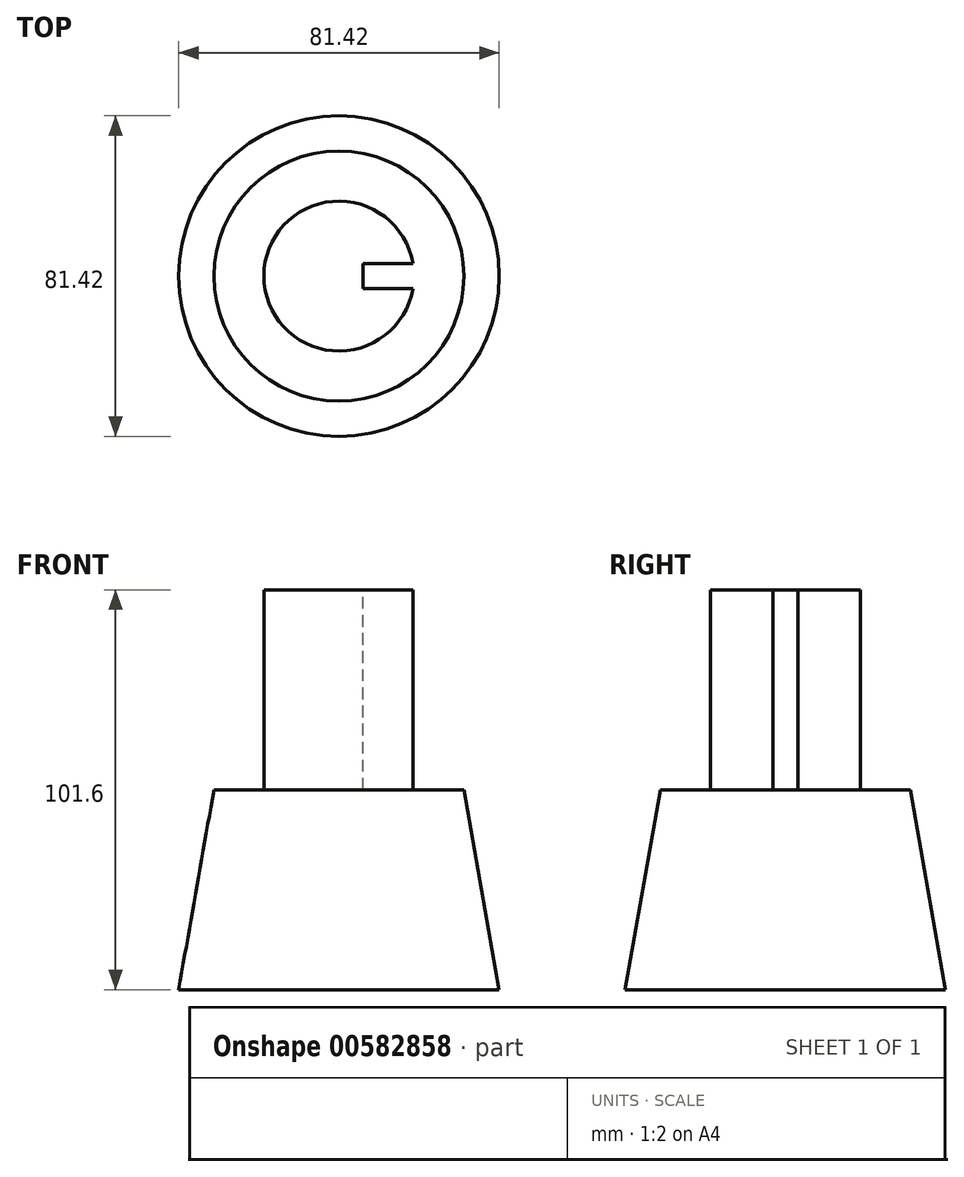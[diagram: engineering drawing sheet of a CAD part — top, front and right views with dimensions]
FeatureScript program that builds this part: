
annotation { "Feature Type Name" : "Feature", "Feature Type Description" : "" }
export const myFeature = defineFeature(function(context is Context, id is Id, definition is map)
    precondition{}
    {
        {
            var Q0;
            Q0=qCreatedBy(makeId("Front.planeOp"),FACE);
            var sketch = newSketch(context, id + "F0", { "sketchPlane" : qUnion([Q0])});
            skLineSegment(sketch, "E0", {"start": v(0, 76.2) * mm, "end": v(0, -76.2) * mm, "construction": true});
            skLineSegment(sketch, "E1", {"start": v(0, -76.2) * mm, "end": v(-25.4, -76.2) * mm});
            skLineSegment(sketch, "E2", {"start": v(-25.4, -76.2) * mm, "end": v(-25.4, 0) * mm});
            skLineSegment(sketch, "E3", {"start": v(-25.4, 0) * mm, "end": v(-22.23, 6.8) * mm});
            skLineSegment(sketch, "E4", {"start": v(-22.23, 6.8) * mm, "end": v(-22.23, 19.5) * mm});
            skArc(sketch, "E5", {"start": v(0, 76.2) * mm, "mid": v(-16.47, 49.95) * mm, "end": v(-22.23, 19.5) * mm});
            skSolve(sketch);
        }
        {
            var Q0;
            Q0=sQuery(id+"F0.wireOp",EDGE,"E5");
            var Q1;
            Q1=sQuery(id+"F0.wireOp",EDGE,"E4");
            var Q2;
            Q2=sQuery(id+"F0.wireOp",EDGE,"E3");
            var Q3;
            Q3=sQuery(id+"F0.wireOp",EDGE,"E2");
            var Q4;
            Q4=sQuery(id+"F0.wireOp",EDGE,"E1");
            var Q5;
            Q5=sQuery(id+"F0.wireOp",EDGE,"E0");
            revolve(context, id + "F1", {"bodyType" : ToolBodyType.SURFACE, "surfaceEntities" : qUnion([Q0, Q1, Q2, Q3, Q4]), "axis" : qUnion([Q5]), "revolveType" : RevolveType.FULL});
        }
        {
            var Q0;
            Q0=makeQuery(id+"F1.opRevolve","SWEPT_FACE",FACE,{"disambiguationData":[OSD([sQuery(id+"F0.wireOp",EDGE,"E1")])]});
            var sketch = newSketch(context, id + "F2", { "sketchPlane" : qUnion([Q0])});
            skCircle(sketch, "E6", {"center": v(0, 0) * mm, "radius": 19.05 * mm});
            skLineSegment(sketch, "E7", {"start": v(18.78, -3.17) * mm, "end": v(6.08, -3.17) * mm});
            skLineSegment(sketch, "E8", {"start": v(6.08, -3.17) * mm, "end": v(6.08, 3.17) * mm});
            skLineSegment(sketch, "E9", {"start": v(6.08, 3.17) * mm, "end": v(18.78, 3.17) * mm});
            skLineSegment(sketch, "E10", {"start": v(18.78, 3.17) * mm, "end": v(18.78, 3.17) * mm});
            skSolve(sketch);
        }
        {
            var Q0;
            {var subQ0=sQuery(id+"F2.wireOp",EDGE,"E7");Q0=makeQuery(id+"F2.imprint","IMPRINT",FACE,{"disambiguationData":[TD([[makeQuery(id+"F2.imprint","IMPRINT",EDGE,{"derivedFrom":subQ0}),1.0]])]});}
            extrude(context, id + "F3", {"entities" : qUnion([Q0]), "oppositeDirection" : true, "depth" : 50.8 * mm, "offsetDistance" : 25.4 * mm});
        }
        {
            var Q0;
            Q0=makeQuery(id+"F3.opExtrude","CAP_FACE",FACE,{"disambiguationData":[OSD([sQuery(id+"F2.wireOp",EDGE,"E6"),sQuery(id+"F2.wireOp",EDGE,"E7"),sQuery(id+"F2.wireOp",EDGE,"E8"),sQuery(id+"F2.wireOp",EDGE,"E9")])],"isStart":false});
            var sketch = newSketch(context, id + "F4", { "sketchPlane" : qUnion([Q0])});
            skCircle(sketch, "E11", {"center": v(0, 0) * mm, "radius": 31.75 * mm});
            skSolve(sketch);
        }
        {
            var Q0;
            Q0 = qSketchRegion(id + "F4", true);
            extrude(context, id + "F5", {"entities" : qUnion([Q0]), "operationType" : NewBodyOperationType.ADD, "depth" : 50.8 * mm, "offsetDistance" : 25.4 * mm, "hasDraft" : true, "draftAngle" : 10 * degree});
        }
    });
